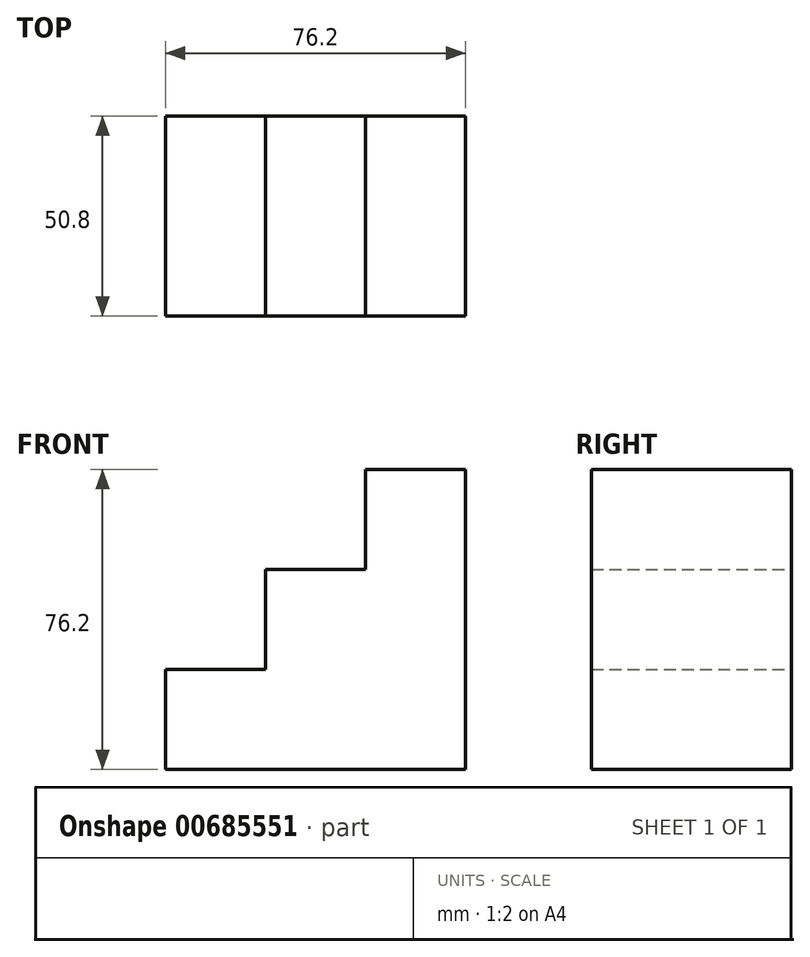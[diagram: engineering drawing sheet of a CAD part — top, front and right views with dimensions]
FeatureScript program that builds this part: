
annotation { "Feature Type Name" : "Feature", "Feature Type Description" : "" }
export const myFeature = defineFeature(function(context is Context, id is Id, definition is map)
    precondition{}
    {
        {
            var Q0;
            Q0=qCreatedBy(makeId("Front.planeOp"),FACE);
            var sketch = newSketch(context, id + "F0", { "sketchPlane" : qUnion([Q0])});
            skLineSegment(sketch, "E0", {"start": v(0, 0) * mm, "end": v(-76.2, 0) * mm});
            skLineSegment(sketch, "E1", {"start": v(-76.2, 0) * mm, "end": v(-76.2, 25.4) * mm});
            skLineSegment(sketch, "E2", {"start": v(-76.2, 25.4) * mm, "end": v(-50.8, 25.4) * mm});
            skLineSegment(sketch, "E3", {"start": v(-50.8, 25.4) * mm, "end": v(-50.8, 50.8) * mm});
            skLineSegment(sketch, "E4", {"start": v(-50.8, 50.8) * mm, "end": v(-25.4, 50.8) * mm});
            skLineSegment(sketch, "E5", {"start": v(-25.4, 50.8) * mm, "end": v(-25.4, 76.2) * mm});
            skLineSegment(sketch, "E6", {"start": v(-25.4, 76.2) * mm, "end": v(0, 76.2) * mm});
            skLineSegment(sketch, "E7", {"start": v(0, 76.2) * mm, "end": v(0, 0) * mm});
            skSolve(sketch);
        }
        {
            var Q0;
            Q0 = qSketchRegion(id + "F0", true);
            extrude(context, id + "F1", {"entities" : qUnion([Q0]), "depth" : 50.8 * mm, "offsetDistance" : 25.4 * mm});
        }
    });
